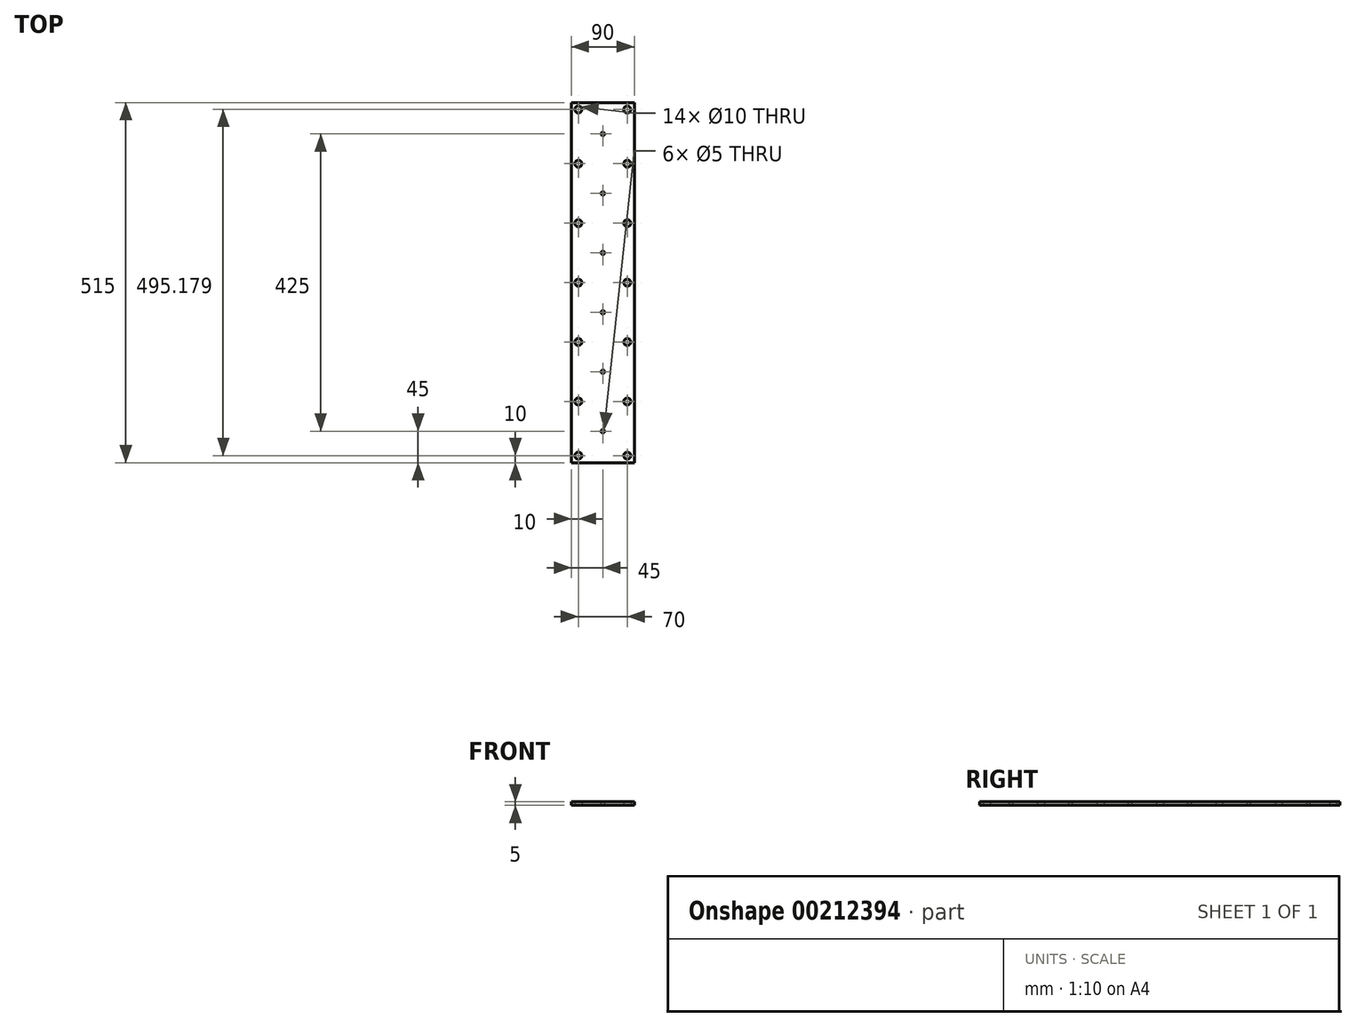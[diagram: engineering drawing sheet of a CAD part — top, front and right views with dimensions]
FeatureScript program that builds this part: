
annotation { "Feature Type Name" : "Feature", "Feature Type Description" : "" }
export const myFeature = defineFeature(function(context is Context, id is Id, definition is map)
    precondition{}
    {
        {
            var Q0;
            Q0=qCreatedBy(makeId("Top.planeOp"),FACE);
            var sketch = newSketch(context, id + "F0", { "sketchPlane" : qUnion([Q0])});
            skCircle(sketch, "E0", {"center": v(-35, 247.68) * mm, "radius": 5 * mm});
            skCircle(sketch, "E1", {"center": v(35, 247.5) * mm, "radius": 5 * mm});
            skCircle(sketch, "E2", {"center": v(-35, 170) * mm, "radius": 5 * mm});
            skCircle(sketch, "E3", {"center": v(35, 170) * mm, "radius": 5 * mm});
            skCircle(sketch, "E4", {"center": v(-35, 85) * mm, "radius": 5 * mm});
            skCircle(sketch, "E5", {"center": v(35, 85) * mm, "radius": 5 * mm});
            skCircle(sketch, "E6.MirrorC", {"center": v(-35, -85) * mm, "radius": 5 * mm});
            skCircle(sketch, "E7.MirrorC", {"center": v(35, -85) * mm, "radius": 5 * mm});
            skCircle(sketch, "E8.MirrorC", {"center": v(35, -170) * mm, "radius": 5 * mm});
            skCircle(sketch, "E9.MirrorC", {"center": v(-35, -170) * mm, "radius": 5 * mm});
            skCircle(sketch, "E10.MirrorC", {"center": v(-35, -247.5) * mm, "radius": 5 * mm});
            skCircle(sketch, "E11.MirrorC", {"center": v(35, -247.5) * mm, "radius": 5 * mm});
            skCircle(sketch, "E12", {"center": v(-35, 0) * mm, "radius": 5 * mm});
            skCircle(sketch, "E13", {"center": v(35, 0) * mm, "radius": 5 * mm});
            skLineSegment(sketch, "E14.bottom", {"start": v(-45, 257.5) * mm, "end": v(45, 257.5) * mm});
            skLineSegment(sketch, "E14.top", {"start": v(-45, -257.5) * mm, "end": v(45, -257.5) * mm});
            skLineSegment(sketch, "E14.left", {"start": v(-45, 257.5) * mm, "end": v(-45, -257.5) * mm});
            skLineSegment(sketch, "E14.right", {"start": v(45, 257.5) * mm, "end": v(45, -257.5) * mm});
            skPoint(sketch, "E14.middle", {"position": v(0, 0) * mm});
            skSolve(sketch);
        }
        {
            var Q0;
            Q0=makeQuery(id+"F0.imprint","IMPRINT",FACE,{"disambiguationData":[TD([[makeQuery(id+"F0.imprint","IMPRINT",EDGE,{"derivedFrom":sQuery(id+"F0.wireOp",EDGE,"E0")}),-1.0]])]});
            extrude(context, id + "F1", {"entities" : qUnion([Q0]), "depth" : 5 * mm});
        }
        {
            var Q0;
            Q0=makeQuery(id+"F1.opExtrude","CAP_FACE",FACE,{"disambiguationData":[OSD([sQuery(id+"F0.wireOp",EDGE,"E0"),sQuery(id+"F0.wireOp",EDGE,"E1"),sQuery(id+"F0.wireOp",EDGE,"E2"),sQuery(id+"F0.wireOp",EDGE,"E3"),sQuery(id+"F0.wireOp",EDGE,"E4"),sQuery(id+"F0.wireOp",EDGE,"E5"),sQuery(id+"F0.wireOp",EDGE,"E6.MirrorC"),sQuery(id+"F0.wireOp",EDGE,"E7.MirrorC"),sQuery(id+"F0.wireOp",EDGE,"E8.MirrorC"),sQuery(id+"F0.wireOp",EDGE,"E9.MirrorC"),sQuery(id+"F0.wireOp",EDGE,"E10.MirrorC"),sQuery(id+"F0.wireOp",EDGE,"E11.MirrorC"),sQuery(id+"F0.wireOp",EDGE,"E12"),sQuery(id+"F0.wireOp",EDGE,"E13"),sQuery(id+"F0.wireOp",EDGE,"E14.bottom"),sQuery(id+"F0.wireOp",EDGE,"E14.top"),sQuery(id+"F0.wireOp",EDGE,"E14.left"),sQuery(id+"F0.wireOp",EDGE,"E14.right")])],"isStart":false});
            var sketch = newSketch(context, id + "F2", { "sketchPlane" : qUnion([Q0])});
            skCircle(sketch, "E15", {"center": v(0, 212.5) * mm, "radius": 2.5 * mm});
            skCircle(sketch, "E16", {"center": v(0, 127.5) * mm, "radius": 2.5 * mm});
            skCircle(sketch, "E17", {"center": v(0, 42.5) * mm, "radius": 2.5 * mm});
            skCircle(sketch, "E18", {"center": v(0, -42.5) * mm, "radius": 2.5 * mm});
            skCircle(sketch, "E19", {"center": v(0, -127.5) * mm, "radius": 2.5 * mm});
            skCircle(sketch, "E20", {"center": v(0, -212.5) * mm, "radius": 2.5 * mm});
            skSolve(sketch);
        }
        {
            var Q0;
            Q0=makeQuery(id+"F2.imprint","IMPRINT",FACE,{"disambiguationData":[TD([[makeQuery(id+"F2.imprint","IMPRINT",EDGE,{"derivedFrom":sQuery(id+"F2.wireOp",EDGE,"E15")}),1.0]])]});
            var Q1;
            Q1=makeQuery(id+"F2.imprint","IMPRINT",FACE,{"disambiguationData":[TD([[makeQuery(id+"F2.imprint","IMPRINT",EDGE,{"derivedFrom":sQuery(id+"F2.wireOp",EDGE,"E16")}),1.0]])]});
            var Q2;
            Q2=makeQuery(id+"F2.imprint","IMPRINT",FACE,{"disambiguationData":[TD([[makeQuery(id+"F2.imprint","IMPRINT",EDGE,{"derivedFrom":sQuery(id+"F2.wireOp",EDGE,"E17")}),1.0]])]});
            var Q3;
            Q3=makeQuery(id+"F2.imprint","IMPRINT",FACE,{"disambiguationData":[TD([[makeQuery(id+"F2.imprint","IMPRINT",EDGE,{"derivedFrom":sQuery(id+"F2.wireOp",EDGE,"E18")}),1.0]])]});
            var Q4;
            Q4=makeQuery(id+"F2.imprint","IMPRINT",FACE,{"disambiguationData":[TD([[makeQuery(id+"F2.imprint","IMPRINT",EDGE,{"derivedFrom":sQuery(id+"F2.wireOp",EDGE,"E19")}),1.0]])]});
            var Q5;
            Q5=makeQuery(id+"F2.imprint","IMPRINT",FACE,{"disambiguationData":[TD([[makeQuery(id+"F2.imprint","IMPRINT",EDGE,{"derivedFrom":sQuery(id+"F2.wireOp",EDGE,"E20")}),1.0]])]});
            extrude(context, id + "F3", {"entities" : qUnion([Q0, Q1, Q2, Q3, Q4, Q5]), "operationType" : NewBodyOperationType.REMOVE, "oppositeDirection" : true, "depth" : 25 * mm});
        }
    });
